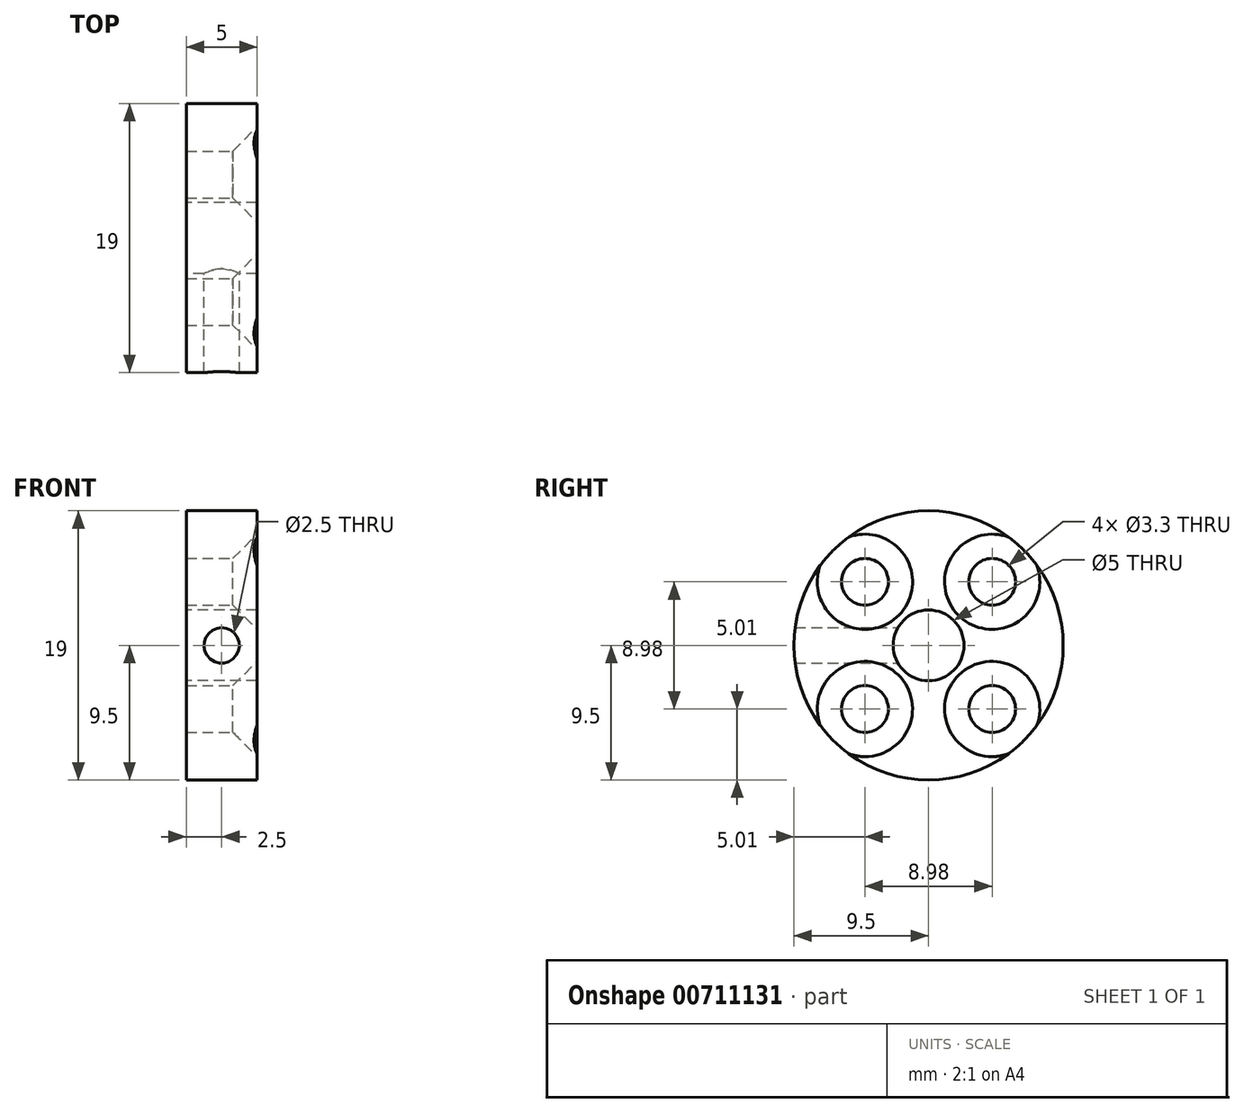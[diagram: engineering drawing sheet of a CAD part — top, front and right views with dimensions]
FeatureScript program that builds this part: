
annotation { "Feature Type Name" : "Feature", "Feature Type Description" : "" }
export const myFeature = defineFeature(function(context is Context, id is Id, definition is map)
    precondition{}
    {
        {
            var Q0;
            Q0=qCreatedBy(makeId("Right.planeOp"),FACE);
            var sketch = newSketch(context, id + "F0", { "sketchPlane" : qUnion([Q0])});
            skCircle(sketch, "E0", {"center": v(0, 0) * mm, "radius": 9.5 * mm});
            skCircle(sketch, "E1", {"center": v(0, 0) * mm, "radius": 2.5 * mm});
            skSolve(sketch);
        }
        {
            var Q0;
            Q0=qSketchRegion(id+"F0",true);
            extrude(context, id + "F1", {"entities" : qUnion([Q0]), "endBound" : BoundingType.SYMMETRIC, "depth" : 5 * mm, "offsetDistance" : 25 * mm});
        }
        {
            var Q0;
            Q0=makeQuery(id+"F1.opExtrude","CAP_FACE",FACE,{"disambiguationData":[OSD([sQuery(id+"F0.wireOp",EDGE,"E0"),sQuery(id+"F0.wireOp",EDGE,"E1")])],"isStart":false});
            var sketch = newSketch(context, id + "F2", { "sketchPlane" : qUnion([Q0])});
            skLineSegment(sketch, "E2", {"start": v(-9.5, 0) * mm, "end": v(0, 0) * mm, "construction": true});
            skLineSegment(sketch, "E3", {"start": v(0, 0) * mm, "end": v(-4.5, 4.5) * mm, "construction": true});
            skCircle(sketch, "E4", {"center": v(-4.5, 4.5) * mm, "radius": 1.5 * mm});
            skCircle(sketch, "E5.1.0", {"center": v(-4.5, -4.5) * mm, "radius": 1.5 * mm});
            skCircle(sketch, "E5.2.0", {"center": v(4.5, -4.5) * mm, "radius": 1.5 * mm});
            skCircle(sketch, "E5.3.0", {"center": v(4.5, 4.5) * mm, "radius": 1.5 * mm});
            skPoint(sketch, "E5.center", {"position": v(0, 0) * mm});
            skSolve(sketch);
        }
        {
            var Q0;
            Q0=qCreatedBy(makeId("Front.planeOp"),FACE);
            var sketch = newSketch(context, id + "F3", { "sketchPlane" : qUnion([Q0])});
            skCircle(sketch, "E6", {"center": v(0, 0) * mm, "radius": 1.25 * mm});
            skSolve(sketch);
        }
        {
            var Q0;
            Q0=qSketchRegion(id+"F3",true);
            extrude(context, id + "F4", {"entities" : qUnion([Q0]), "operationType" : NewBodyOperationType.REMOVE, "endBound" : BoundingType.THROUGH_ALL, "depth" : 25 * mm, "offsetDistance" : 25 * mm});
        }
        {
            var Q0;
            Q0=sQuery(id+"F2.wireOp",VERTEX,"E4.center");
            var Q1;
            Q1=sQuery(id+"F2.wireOp",VERTEX,"E5.3.0.center");
            var Q2;
            Q2=sQuery(id+"F2.wireOp",VERTEX,"E5.2.0.center");
            var Q3;
            Q3=sQuery(id+"F2.wireOp",VERTEX,"E5.1.0.center");
            var Q4;
            Q4=makeQuery(id+"F1.opExtrude","SWEPT_BODY",BODY,{"disambiguationData":[OSD([sQuery(id+"F0.wireOp",EDGE,"E0"),sQuery(id+"F0.wireOp",EDGE,"E1")])]});
            hole(context, id + "F5", {"style" : HoleStyle.C_SINK, "endStyle" : HoleEndStyle.THROUGH, "standardTappedOrClearance" : lookupTablePath({ "standard" : "ISO", "fit" : "Normal", "size" : "M3", "type" : "Clearance" }), "standardBlindInLast" : lookupTablePath({ "fit" : "Standard", "standard" : "ISO", "size" : "M3", "type" : "Clearance" }), "holeDiameter" : 3.3 * mm, "cSinkDiameter" : 6.72 * mm, "cSinkAngle" : 90 * degree, "majorDiameter" : 5 * mm, "isTappedThrough" : true, "tappedDepth" : 12 * mm, "tapClearance" : 3, "locations" : qUnion([Q0, Q1, Q2, Q3]), "scope" : qUnion([Q4])});
        }
    });
